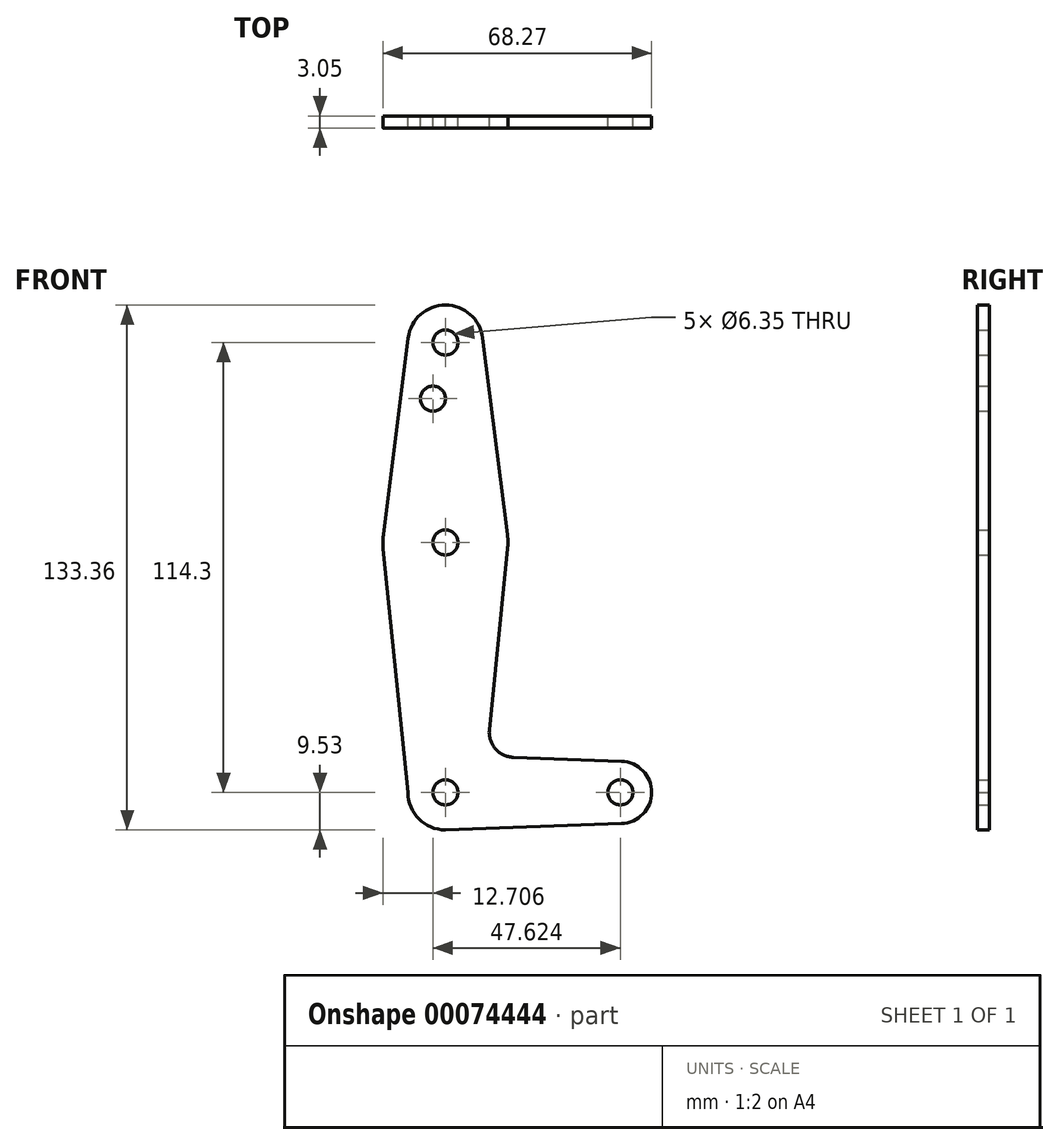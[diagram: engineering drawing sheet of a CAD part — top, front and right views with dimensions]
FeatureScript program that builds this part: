
annotation { "Feature Type Name" : "Feature", "Feature Type Description" : "" }
export const myFeature = defineFeature(function(context is Context, id is Id, definition is map)
    precondition{}
    {
        {
            var Q0;
            Q0=qCreatedBy(makeId("Front.planeOp"),FACE);
            var sketch = newSketch(context, id + "F0", { "sketchPlane" : qUnion([Q0])});
            skLineSegment(sketch, "E0", {"start": v(0, 114.3) * mm, "end": v(0, 0) * mm, "construction": true});
            skLineSegment(sketch, "E1", {"start": v(0, 0) * mm, "end": v(44.45, 0) * mm, "construction": true});
            skCircle(sketch, "E2", {"center": v(0, 114.3) * mm, "radius": 9.53 * mm});
            skCircle(sketch, "E3", {"center": v(0, 0) * mm, "radius": 9.52 * mm});
            skCircle(sketch, "E4", {"center": v(44.45, 0) * mm, "radius": 7.94 * mm});
            skCircle(sketch, "E5", {"center": v(0, 63.5) * mm, "radius": 15.88 * mm});
            skLineSegment(sketch, "E6", {"start": v(0, -9.52) * mm, "end": v(44.73, -7.93) * mm});
            skLineSegment(sketch, "E7", {"start": v(17.26, 8.91) * mm, "end": v(44.73, 7.93) * mm});
            skLineSegment(sketch, "E8", {"start": v(-15.75, 65.48) * mm, "end": v(-9.45, 115.5) * mm});
            skLineSegment(sketch, "E9", {"start": v(9.45, 115.5) * mm, "end": v(15.75, 65.48) * mm});
            skLineSegment(sketch, "E10", {"start": v(15.8, 61.91) * mm, "end": v(11.17, 15.9) * mm});
            skLineSegment(sketch, "E11", {"start": v(-9.52, 0) * mm, "end": v(-15.8, 61.9) * mm});
            skCircle(sketch, "E12", {"center": v(0, 114.3) * mm, "radius": 3.18 * mm});
            skCircle(sketch, "E13", {"center": v(0, 0) * mm, "radius": 3.18 * mm});
            skCircle(sketch, "E14", {"center": v(0, 63.5) * mm, "radius": 3.18 * mm});
            skCircle(sketch, "E15", {"center": v(44.45, 0) * mm, "radius": 3.18 * mm});
            skCircle(sketch, "E16", {"center": v(-3.17, 100.03) * mm, "radius": 3.18 * mm});
            skPoint(sketch, "E16.first.point", {"position": v(0, 100.11) * mm});
            skPoint(sketch, "E16.second.point", {"position": v(-6.34, 100.2) * mm});
            skPoint(sketch, "E16.third.point", {"position": v(-3, 96.85) * mm});
            skLineSegment(sketch, "E17", {"start": v(0, 63.5) * mm, "end": v(-28.36, 63.5) * mm});
            skArc(sketch, "E18.filletArc", {"start": v(11.17, 15.9) * mm, "mid": v(12.7, 11.08) * mm, "end": v(17.26, 8.91) * mm});
            skSolve(sketch);
        }
        {
            var Q0;
            {var subQ1=sQuery(id+"F0.wireOp",EDGE,"E8");Q0=makeQuery(id+"F0.imprint","IMPRINT",FACE,{"disambiguationData":[TD([[makeQuery(id+"F0.imprint","IMPRINT",EDGE,{"derivedFrom":subQ1}),-1.0]])]});}
            var Q1;
            Q1=makeQuery(id+"F0.imprint","IMPRINT",FACE,{"disambiguationData":[TD([[makeQuery(id+"F0.imprint","IMPRINT",EDGE,{"derivedFrom":sQuery(id+"F0.wireOp",EDGE,"E14")}),-1.0]])]});
            var Q2;
            {var subQ3=sQuery(id+"F0.wireOp",EDGE,"E11");Q2=makeQuery(id+"F0.imprint","IMPRINT",FACE,{"disambiguationData":[TD([[makeQuery(id+"F0.imprint","IMPRINT",EDGE,{"derivedFrom":subQ3}),-1.0]])]});}
            var Q3;
            Q3=makeQuery(id+"F0.imprint","IMPRINT",FACE,{"disambiguationData":[TD([[makeQuery(id+"F0.imprint","IMPRINT",EDGE,{"derivedFrom":sQuery(id+"F0.wireOp",EDGE,"E12")}),-1.0]])]});
            var Q4;
            {var subQ2=sQuery(id+"F0.wireOp",EDGE,"E3");var subQ4=sQuery(id+"F0.wireOp",EDGE,"E6");var subQ7=makeQuery(id+"F0.imprint","INTERSECT",VERTEX,{"disambiguationData":[OD(1.0)],"derivedFrom":[subQ2,subQ4]});Q4=makeQuery(id+"F0.imprint","IMPRINT",FACE,{"disambiguationData":[TD([[makeQuery(id+"F0.imprint","IMPRINT",EDGE,{"disambiguationData":[TD([[subQ7,-1.0]])],"derivedFrom":subQ2}),-1.0]])]});}
            var Q5;
            Q5=makeQuery(id+"F0.imprint","IMPRINT",FACE,{"disambiguationData":[TD([[makeQuery(id+"F0.imprint","IMPRINT",EDGE,{"derivedFrom":sQuery(id+"F0.wireOp",EDGE,"E13")}),-1.0]])]});
            var Q6;
            Q6=makeQuery(id+"F0.imprint","IMPRINT",FACE,{"disambiguationData":[TD([[makeQuery(id+"F0.imprint","IMPRINT",EDGE,{"derivedFrom":sQuery(id+"F0.wireOp",EDGE,"E15")}),-1.0]])]});
            extrude(context, id + "F1", {"entities" : qUnion([Q0, Q1, Q2, Q3, Q4, Q5, Q6]), "depth" : 3.05 * mm});
        }
    });
